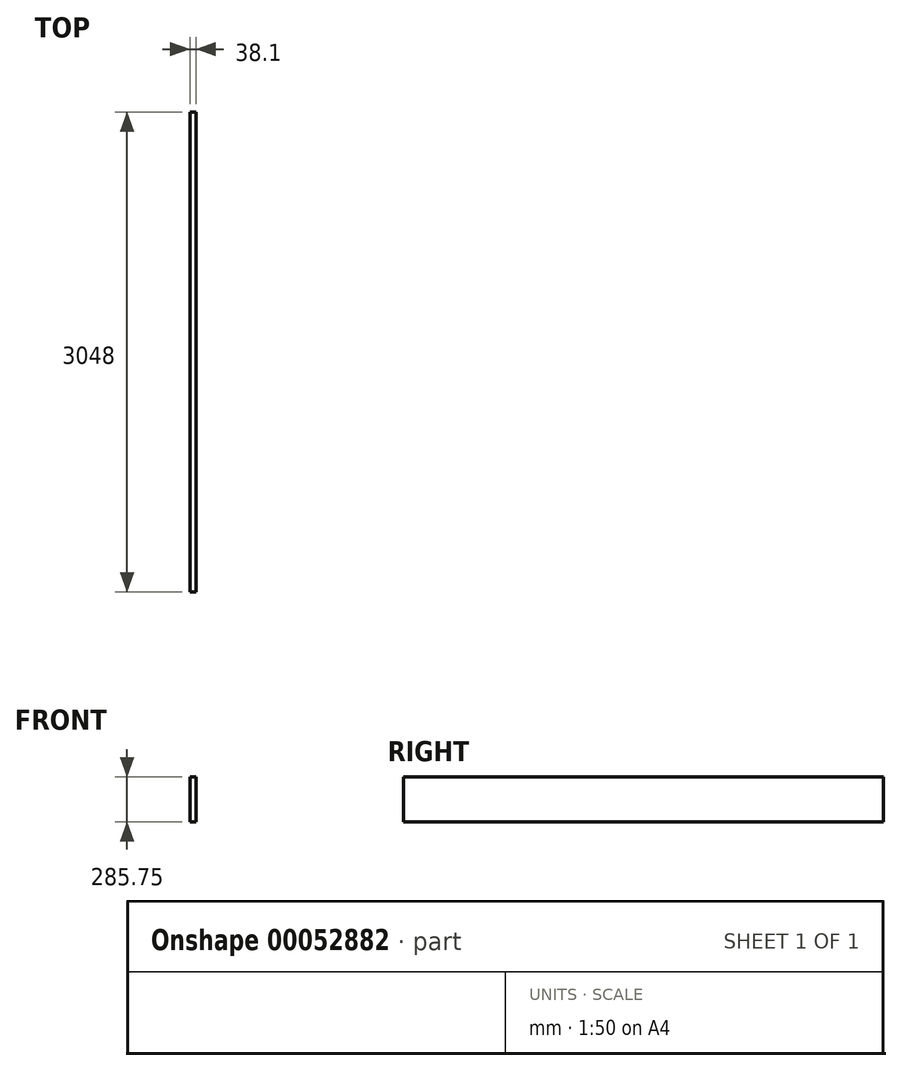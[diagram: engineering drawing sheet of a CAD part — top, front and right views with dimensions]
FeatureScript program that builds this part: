
annotation { "Feature Type Name" : "Feature", "Feature Type Description" : "" }
export const myFeature = defineFeature(function(context is Context, id is Id, definition is map)
    precondition{}
    {
        {
            var Q0;
            Q0=qCreatedBy(makeId("Front.planeOp"),FACE);
            var sketch = newSketch(context, id + "F0", { "sketchPlane" : qUnion([Q0])});
            skLineSegment(sketch, "E0.bottom", {"start": v(0, 0) * mm, "end": v(38.1, 0) * mm});
            skLineSegment(sketch, "E0.top", {"start": v(0, -285.75) * mm, "end": v(38.1, -285.75) * mm});
            skLineSegment(sketch, "E0.left", {"start": v(0, 0) * mm, "end": v(0, -285.75) * mm});
            skLineSegment(sketch, "E0.right", {"start": v(38.1, 0) * mm, "end": v(38.1, -285.75) * mm});
            skSolve(sketch);
        }
        {
            var Q0;
            Q0 = qSketchRegion(id + "F0", true);
            extrude(context, id + "F1", {"entities" : qUnion([Q0]), "depth" : 3048 * mm});
        }
    });
